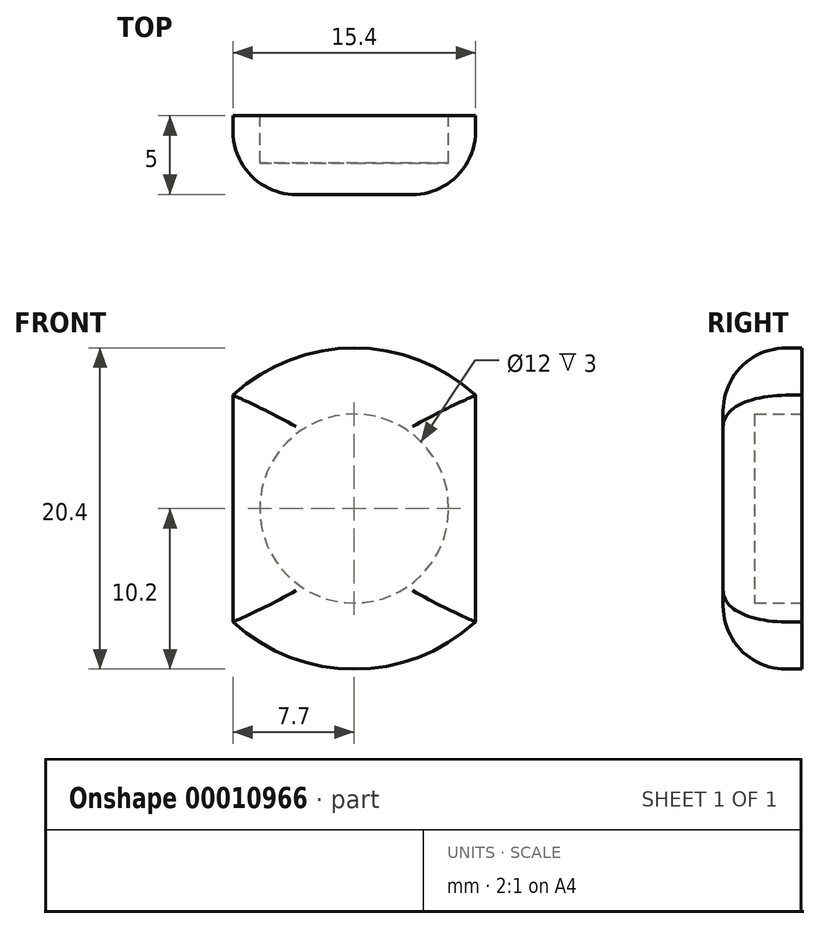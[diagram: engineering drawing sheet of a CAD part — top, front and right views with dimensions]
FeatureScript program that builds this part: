
annotation { "Feature Type Name" : "Feature", "Feature Type Description" : "" }
export const myFeature = defineFeature(function(context is Context, id is Id, definition is map)
    precondition{}
    {
        {
            var Q0;
            Q0=qCreatedBy(makeId("Front.planeOp"),FACE);
            var sketch = newSketch(context, id + "F0", { "sketchPlane" : qUnion([Q0])});
            skLineSegment(sketch, "E0.bottom", {"start": v(7.7, -7.2) * mm, "end": v(-7.7, -7.2) * mm, "construction": true});
            skLineSegment(sketch, "E0.top", {"start": v(7.7, 7.2) * mm, "end": v(-7.7, 7.2) * mm, "construction": true});
            skLineSegment(sketch, "E0.left", {"start": v(7.7, -7.2) * mm, "end": v(7.7, 7.2) * mm});
            skLineSegment(sketch, "E0.right", {"start": v(-7.7, -7.2) * mm, "end": v(-7.7, 7.2) * mm});
            skLineSegment(sketch, "E1", {"start": v(0, -7.2) * mm, "end": v(0, 0) * mm, "construction": true});
            skLineSegment(sketch, "E2", {"start": v(0, 0) * mm, "end": v(0, 7.2) * mm, "construction": true});
            skArc(sketch, "E3", {"start": v(-7.7, -7.2) * mm, "mid": v(0, -10.2) * mm, "end": v(7.7, -7.2) * mm});
            skArc(sketch, "E4", {"start": v(7.7, 7.2) * mm, "mid": v(0, 10.2) * mm, "end": v(-7.7, 7.2) * mm});
            skSolve(sketch);
        }
        {
            var Q0;
            Q0 = qSketchRegion(id + "F0", true);
            extrude(context, id + "F1", {"entities" : qUnion([Q0]), "depth" : 5 * mm});
        }
        {
            var Q0;
            Q0=makeQuery(id+"F1.opExtrude","CAP_EDGE",EDGE,{"disambiguationData":[OSD([sQuery(id+"F0.wireOp",EDGE,"E0.right")])],"isStart":false});
            var Q1;
            Q1=makeQuery(id+"F1.opExtrude","CAP_EDGE",EDGE,{"disambiguationData":[OSD([sQuery(id+"F0.wireOp",EDGE,"E3")])],"isStart":false});
            var Q2;
            Q2=makeQuery(id+"F1.opExtrude","CAP_EDGE",EDGE,{"disambiguationData":[OSD([sQuery(id+"F0.wireOp",EDGE,"E0.left")])],"isStart":false});
            var Q3;
            Q3=makeQuery(id+"F1.opExtrude","CAP_EDGE",EDGE,{"disambiguationData":[OSD([sQuery(id+"F0.wireOp",EDGE,"E4")])],"isStart":false});
            fillet(context, id + "F2", {"entities" : qUnion([Q0, Q1, Q2, Q3]), "radius" : 4 * mm, "tangentPropagation" : true, "allowEdgeOverflow" : false});
        }
        {
            var Q0;
            Q0=makeQuery(id+"F1.opExtrude","CAP_FACE",FACE,{"disambiguationData":[OSD([sQuery(id+"F0.wireOp",EDGE,"E0.left"),sQuery(id+"F0.wireOp",EDGE,"E0.right"),sQuery(id+"F0.wireOp",EDGE,"E3"),sQuery(id+"F0.wireOp",EDGE,"E4")])],"isStart":true});
            var sketch = newSketch(context, id + "F3", { "sketchPlane" : qUnion([Q0])});
            skCircle(sketch, "E5", {"center": v(0, 0) * mm, "radius": 6 * mm});
            skSolve(sketch);
        }
        {
            var Q0;
            Q0 = qSketchRegion(id + "F3", true);
            extrude(context, id + "F4", {"entities" : qUnion([Q0]), "operationType" : NewBodyOperationType.REMOVE, "oppositeDirection" : true, "depth" : 3 * mm});
        }
    });
